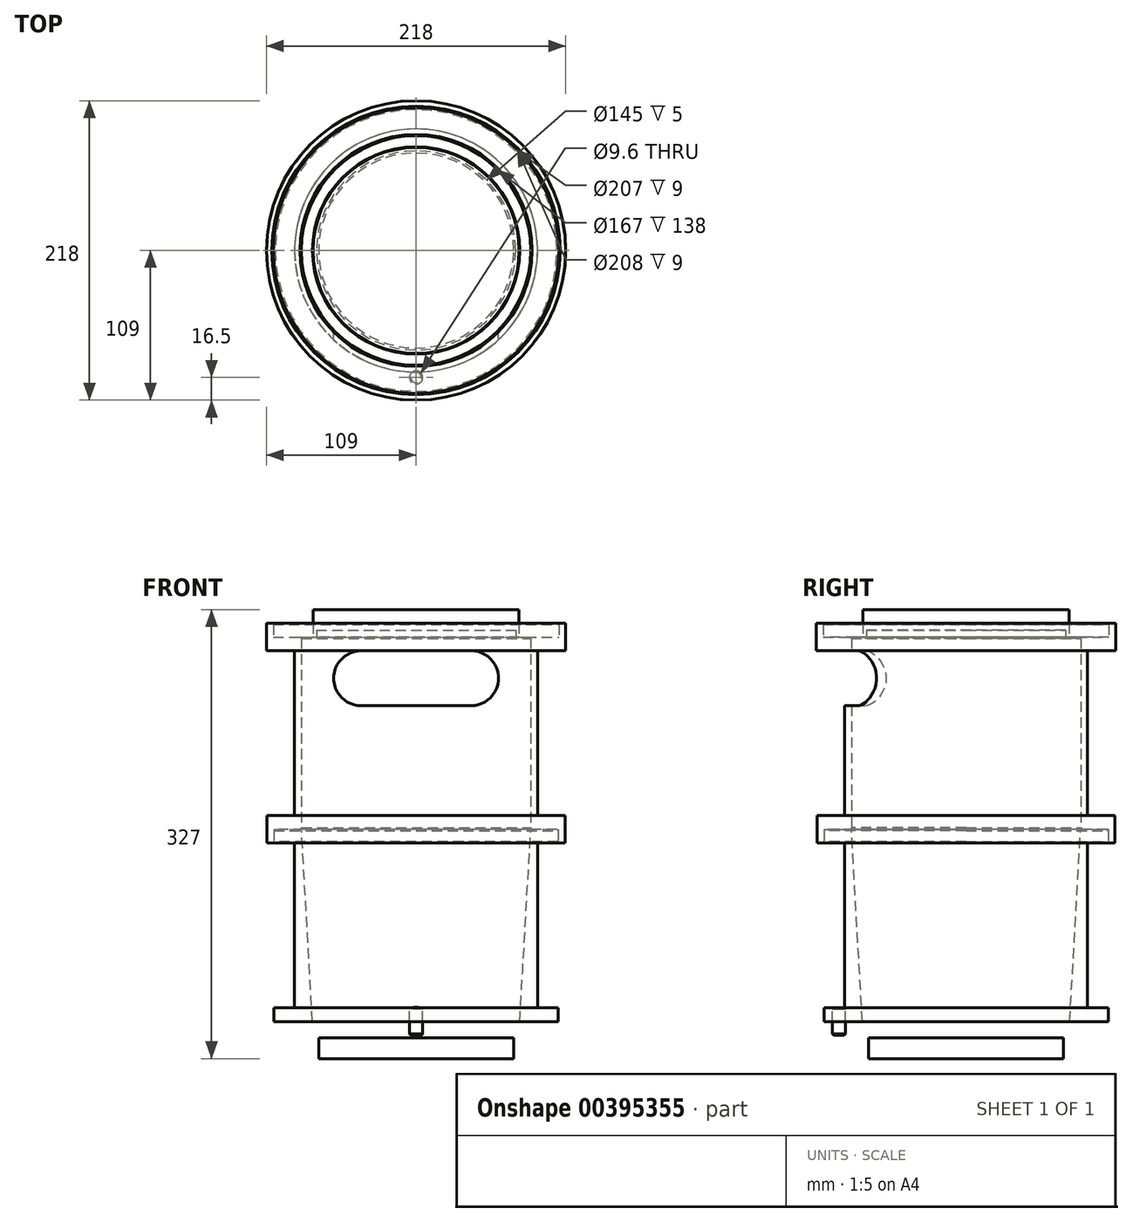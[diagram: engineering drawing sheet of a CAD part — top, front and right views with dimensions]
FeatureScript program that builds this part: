
annotation { "Feature Type Name" : "Feature", "Feature Type Description" : "" }
export const myFeature = defineFeature(function(context is Context, id is Id, definition is map)
    precondition{}
    {
        {
            var Q0;
            Q0=qCreatedBy(makeId("Top.planeOp"),FACE);
            var sketch = newSketch(context, id + "F0", { "sketchPlane" : qUnion([Q0])});
            skCircle(sketch, "E0", {"center": v(0, 0) * mm, "radius": 103.5 * mm});
            skCircle(sketch, "E1", {"center": v(0, 0) * mm, "radius": 76 * mm});
            skCircle(sketch, "E2", {"center": v(0, 0) * mm, "radius": 92.5 * mm, "construction": true});
            skCircle(sketch, "E3", {"center": v(0, 92.5) * mm, "radius": 5 * mm});
            skCircle(sketch, "E4.1.0", {"center": v(-80.1, 46.25) * mm, "radius": 5 * mm});
            skCircle(sketch, "E4.2.0", {"center": v(-80.1, -46.25) * mm, "radius": 5 * mm});
            skCircle(sketch, "E4.3.0", {"center": v(0, -92.5) * mm, "radius": 5 * mm});
            skCircle(sketch, "E4.4.0", {"center": v(80.1, -46.25) * mm, "radius": 5 * mm});
            skCircle(sketch, "E4.5.0", {"center": v(80.1, 46.25) * mm, "radius": 5 * mm});
            skSolve(sketch);
        }
        {
            var Q0;
            Q0 = qSketchRegion(id + "F0", true);
            extrude(context, id + "F1", {"entities" : qUnion([Q0]), "depth" : 12 * mm});
        }
        {
            var Q0;
            Q0=qCreatedBy(makeId("Front.planeOp"),FACE);
            var sketch = newSketch(context, id + "F2", { "sketchPlane" : qUnion([Q0])});
            skLineSegment(sketch, "E5", {"start": v(-103.5, 152) * mm, "end": v(-65, 152) * mm});
            skLineSegment(sketch, "E6", {"start": v(-65, 152) * mm, "end": v(-65, 12) * mm});
            skLineSegment(sketch, "E7", {"start": v(-65, 12) * mm, "end": v(-103.5, 12) * mm});
            skLineSegment(sketch, "E8", {"start": v(-103.5, 12) * mm, "end": v(-103.5, 22) * mm});
            skLineSegment(sketch, "E9", {"start": v(-103.5, 22) * mm, "end": v(-88.5, 22) * mm});
            skLineSegment(sketch, "E10", {"start": v(-88.5, 22) * mm, "end": v(-88.5, 142) * mm});
            skLineSegment(sketch, "E11", {"start": v(-88.5, 142) * mm, "end": v(-103.5, 142) * mm});
            skLineSegment(sketch, "E12", {"start": v(-103.5, 142) * mm, "end": v(-103.5, 152) * mm});
            skLineSegment(sketch, "E13", {"start": v(0, 0) * mm, "end": v(0, 194.8) * mm, "construction": true});
            skSolve(sketch);
        }
        {
            var Q0;
            Q0=makeQuery(id+"F2.imprint","IMPRINT",FACE,{"disambiguationData":[TD([[makeQuery(id+"F2.imprint","IMPRINT",EDGE,{"derivedFrom":sQuery(id+"F2.wireOp",EDGE,"E5")}),-1.0]])]});
            var Q1;
            Q1 = qConstructionFilter(qBodyType(qCreatedBy(id + "F2" ,EDGE), BodyType.WIRE), ConstructionObject.NO);
            var Q2;
            Q2=sQuery(id+"F2.wireOp",EDGE,"E13");
            revolve(context, id + "F3", {"entities" : qUnion([Q0]), "surfaceEntities" : qUnion([Q1]), "axis" : qUnion([Q2]), "revolveType" : RevolveType.FULL});
        }
        {
            var Q0;
            Q0=qCreatedBy(makeId("Front.planeOp"),FACE);
            var sketch = newSketch(context, id + "F4", { "sketchPlane" : qUnion([Q0])});
            skLineSegment(sketch, "E14", {"start": v(0, 12) * mm, "end": v(0, 152) * mm});
            skLineSegment(sketch, "E15", {"start": v(0, 152) * mm, "end": v(-83.5, 152) * mm});
            skLineSegment(sketch, "E16", {"start": v(-83.5, 152) * mm, "end": v(-75.5, 12) * mm});
            skLineSegment(sketch, "E17", {"start": v(-75.5, 12) * mm, "end": v(0, 12) * mm});
            skSolve(sketch);
        }
        {
            var Q0;
            Q0 = qSketchRegion(id + "F4", true);
            var Q1;
            Q1=sQuery(id+"F4.wireOp",EDGE,"E14");
            revolve(context, id + "F5", {"operationType" : NewBodyOperationType.REMOVE, "entities" : qUnion([Q0]), "axis" : qUnion([Q1]), "revolveType" : RevolveType.FULL, "oppositeDirection" : true});
        }
        {
            var Q0;
            Q0=qCreatedBy(makeId("Front.planeOp"),FACE);
            var sketch = newSketch(context, id + "F6", { "sketchPlane" : qUnion([Q0])});
            skLineSegment(sketch, "E18", {"start": v(-108.5, 142) * mm, "end": v(-103.5, 142) * mm});
            skLineSegment(sketch, "E19", {"start": v(-103.5, 142) * mm, "end": v(-103.5, 152) * mm});
            skLineSegment(sketch, "E20", {"start": v(-103.5, 152) * mm, "end": v(-83.5, 152) * mm});
            skLineSegment(sketch, "E21", {"start": v(-83.5, 152) * mm, "end": v(-83.5, 292) * mm});
            skLineSegment(sketch, "E22", {"start": v(-83.5, 292) * mm, "end": v(-104, 292) * mm});
            skLineSegment(sketch, "E23", {"start": v(-109, 282) * mm, "end": v(-88.5, 282) * mm});
            skLineSegment(sketch, "E24", {"start": v(-88.5, 282) * mm, "end": v(-88.5, 162) * mm});
            skLineSegment(sketch, "E25", {"start": v(-88.5, 162) * mm, "end": v(-108.5, 162) * mm});
            skLineSegment(sketch, "E26", {"start": v(-108.5, 162) * mm, "end": v(-108.5, 142) * mm});
            skLineSegment(sketch, "E27.top", {"start": v(-104, 302) * mm, "end": v(-109, 302) * mm});
            skLineSegment(sketch, "E27.left", {"start": v(-104, 292) * mm, "end": v(-104, 302) * mm});
            skLineSegment(sketch, "E27.right", {"start": v(-109, 282) * mm, "end": v(-109, 302) * mm});
            skLineSegment(sketch, "E28", {"start": v(0, 0) * mm, "end": v(0, 407.54) * mm, "construction": true});
            skSolve(sketch);
        }
        {
            var Q0;
            Q0 = qSketchRegion(id + "F6", true);
            var Q1;
            Q1=sQuery(id+"F6.wireOp",EDGE,"E28");
            revolve(context, id + "F7", {"entities" : qUnion([Q0]), "axis" : qUnion([Q1]), "revolveType" : RevolveType.FULL});
        }
        {
            var Q0;
            Q0=makeQuery(id+"F7.opRevolve","SWEPT_FACE",FACE,{"disambiguationData":[OSD([sQuery(id+"F6.wireOp",EDGE,"E22")])]});
            var sketch = newSketch(context, id + "F8", { "sketchPlane" : qUnion([Q0])});
            skCircle(sketch, "E29", {"center": v(0, 0) * mm, "radius": 75 * mm});
            skSolve(sketch);
        }
        {
            var Q0;
            Q0 = qSketchRegion(id + "F8", true);
            extrude(context, id + "F9", {"entities" : qUnion([Q0]), "depth" : 20 * mm});
        }
        {
            var Q0;
            Q0=qCreatedBy(makeId("Front.planeOp"),FACE);
            var sketch = newSketch(context, id + "F10", { "sketchPlane" : qUnion([Q0])});
            skLineSegment(sketch, "E30.bottom", {"start": v(40, 282) * mm, "end": v(-40, 282) * mm});
            skLineSegment(sketch, "E30.top", {"start": v(40, 242) * mm, "end": v(-40, 242) * mm});
            skArc(sketch, "E31", {"start": v(40, 242) * mm, "mid": v(60, 262) * mm, "end": v(40, 282) * mm});
            skArc(sketch, "E32", {"start": v(-40, 282) * mm, "mid": v(-60, 262) * mm, "end": v(-40, 242) * mm});
            skLineSegment(sketch, "E33", {"start": v(-40, 262) * mm, "end": v(40, 262) * mm, "construction": true});
            skPoint(sketch, "E34", {"position": v(0, 262) * mm});
            skSolve(sketch);
        }
        {
            var Q0;
            Q0 = qSketchRegion(id + "F10", true);
            extrude(context, id + "F11", {"entities" : qUnion([Q0]), "operationType" : NewBodyOperationType.REMOVE, "endBound" : BoundingType.THROUGH_ALL, "depth" : 200 * mm});
        }
        {
            var Q0;
            Q0=makeQuery(id+"F9.opExtrude","CAP_FACE",FACE,{"disambiguationData":[OSD([sQuery(id+"F8.wireOp",EDGE,"E29")])],"isStart":true});
            var sketch = newSketch(context, id + "F12", { "sketchPlane" : qUnion([Q0])});
            skCircle(sketch, "E35", {"center": v(0, 0) * mm, "radius": 72.5 * mm});
            skSolve(sketch);
        }
        {
            var Q0;
            Q0 = qSketchRegion(id + "F12", true);
            extrude(context, id + "F13", {"entities" : qUnion([Q0]), "operationType" : NewBodyOperationType.REMOVE, "oppositeDirection" : true, "depth" : 5 * mm});
        }
        {
            var Q0;
            Q0=qCreatedBy(makeId("Top.planeOp"),FACE);
            var sketch = newSketch(context, id + "F14", { "sketchPlane" : qUnion([Q0])});
            skCircle(sketch, "E36", {"center": v(0, 0) * mm, "radius": 71 * mm});
            skSolve(sketch);
        }
        {
            var Q0;
            Q0 = qSketchRegion(id + "F14", true);
            extrude(context, id + "F15", {"entities" : qUnion([Q0]), "oppositeDirection" : true, "depth" : 15 * mm});
        }
        {
            var Q0;
            Q0=makeQuery(id+"F1.opExtrude","SWEPT_BODY",BODY,{"disambiguationData":[OSD([sQuery(id+"F0.wireOp",EDGE,"E0"),sQuery(id+"F0.wireOp",EDGE,"E1"),sQuery(id+"F0.wireOp",EDGE,"E3"),sQuery(id+"F0.wireOp",EDGE,"E4.1.0"),sQuery(id+"F0.wireOp",EDGE,"E4.2.0"),sQuery(id+"F0.wireOp",EDGE,"E4.3.0"),sQuery(id+"F0.wireOp",EDGE,"E4.4.0"),sQuery(id+"F0.wireOp",EDGE,"E4.5.0")])]});
            deleteBodies(context, id + "F16", {"entities" : qUnion([Q0])});
        }
        {
            var Q0;
            Q0=makeQuery(id+"F3.opRevolve","SWEPT_EDGE",EDGE,{"disambiguationData":[OSD([sQuery(id+"F2.wireOp",EDGE,"E5"),sQuery(id+"F2.wireOp",EDGE,"E12")])]});
            chamfer(context, id + "F17", {"entities" : qUnion([Q0]), "width" : 1 * mm, "tangentPropagation" : true});
        }
        {
            var Q0;
            Q0=makeQuery(id+"F7.opRevolve","SWEPT_EDGE",EDGE,{"disambiguationData":[OSD([sQuery(id+"F6.wireOp",EDGE,"E18"),sQuery(id+"F6.wireOp",EDGE,"E19")])]});
            var Q1;
            Q1=makeQuery(id+"F7.opRevolve","SWEPT_EDGE",EDGE,{"disambiguationData":[OSD([sQuery(id+"F6.wireOp",EDGE,"E20"),sQuery(id+"F6.wireOp",EDGE,"E21")])]});
            chamfer(context, id + "F18", {"entities" : qUnion([Q0, Q1]), "width" : 1 * mm, "tangentPropagation" : true});
        }
        {
            var Q0;
            Q0=makeQuery(id+"F7.opRevolve","SWEPT_EDGE",EDGE,{"disambiguationData":[OSD([sQuery(id+"F6.wireOp",EDGE,"E27.top"),sQuery(id+"F6.wireOp",EDGE,"E27.left")])]});
            var Q1;
            Q1=makeQuery(id+"F7.opRevolve","SWEPT_EDGE",EDGE,{"disambiguationData":[OSD([sQuery(id+"F6.wireOp",EDGE,"E21"),sQuery(id+"F6.wireOp",EDGE,"E22")])]});
            chamfer(context, id + "F19", {"entities" : qUnion([Q0, Q1]), "width" : 1 * mm, "tangentPropagation" : true});
        }
        {
            var Q0;
            Q0=makeQuery(id+"F3.opRevolve","SWEPT_FACE",FACE,{"disambiguationData":[OSD([sQuery(id+"F2.wireOp",EDGE,"E7")])]});
            var sketch = newSketch(context, id + "F20", { "sketchPlane" : qUnion([Q0])});
            skCircle(sketch, "E37", {"center": v(0, 92.5) * mm, "radius": 4.8 * mm});
            skCircle(sketch, "E38", {"center": v(0, 0) * mm, "radius": 92.5 * mm, "construction": true});
            skSolve(sketch);
        }
        {
            var Q0;
            Q0=sQuery(id+"F20.wireOp",VERTEX,"E37.center");
            var Q1;
            Q1=makeQuery(id+"F3.opRevolve","SWEPT_BODY",BODY,{"disambiguationData":[OSD([sQuery(id+"F2.wireOp",EDGE,"E5"),sQuery(id+"F2.wireOp",EDGE,"E6"),sQuery(id+"F2.wireOp",EDGE,"E7"),sQuery(id+"F2.wireOp",EDGE,"E8"),sQuery(id+"F2.wireOp",EDGE,"E9"),sQuery(id+"F2.wireOp",EDGE,"E10"),sQuery(id+"F2.wireOp",EDGE,"E11"),sQuery(id+"F2.wireOp",EDGE,"E12")])]});
            hole(context, id + "F21", {"style" : HoleStyle.SIMPLE, "endStyle" : HoleEndStyle.BLIND, "holeDiameter" : 9.6 * mm, "holeDepth" : 10 * mm, "isTappedThrough" : true, "tappedDepth" : 12 * mm, "tapClearance" : 3, "locations" : qUnion([Q0]), "scope" : qUnion([Q1]), "startStyle" : HoleStartStyle.SKETCH});
        }
        {
            var Q0;
            Q0=makeQuery(id+"F3.opRevolve","SWEPT_FACE",FACE,{"disambiguationData":[OSD([sQuery(id+"F2.wireOp",EDGE,"E9")])]});
            var sketch = newSketch(context, id + "F22", { "sketchPlane" : qUnion([Q0])});
            skCircle(sketch, "E39", {"center": v(0, -92.5) * mm, "radius": 4.8 * mm});
            skSolve(sketch);
        }
        {
            var Q0;
            Q0 = qSketchRegion(id + "F22", true);
            extrude(context, id + "F23", {"entities" : qUnion([Q0]), "oppositeDirection" : true, "depth" : 20 * mm});
        }
        {
            var Q0;
            Q0=makeQuery(id+"F23.opExtrude","CAP_EDGE",EDGE,{"disambiguationData":[OSD([sQuery(id+"F22.wireOp",EDGE,"E39")])],"isStart":false});
            var Q1;
            Q1=makeQuery(id+"F23.opExtrude","CAP_EDGE",EDGE,{"disambiguationData":[OSD([sQuery(id+"F22.wireOp",EDGE,"E39")])],"isStart":true});
            chamfer(context, id + "F24", {"entities" : qUnion([Q0, Q1]), "width" : 1 * mm, "tangentPropagation" : true});
        }
    });
